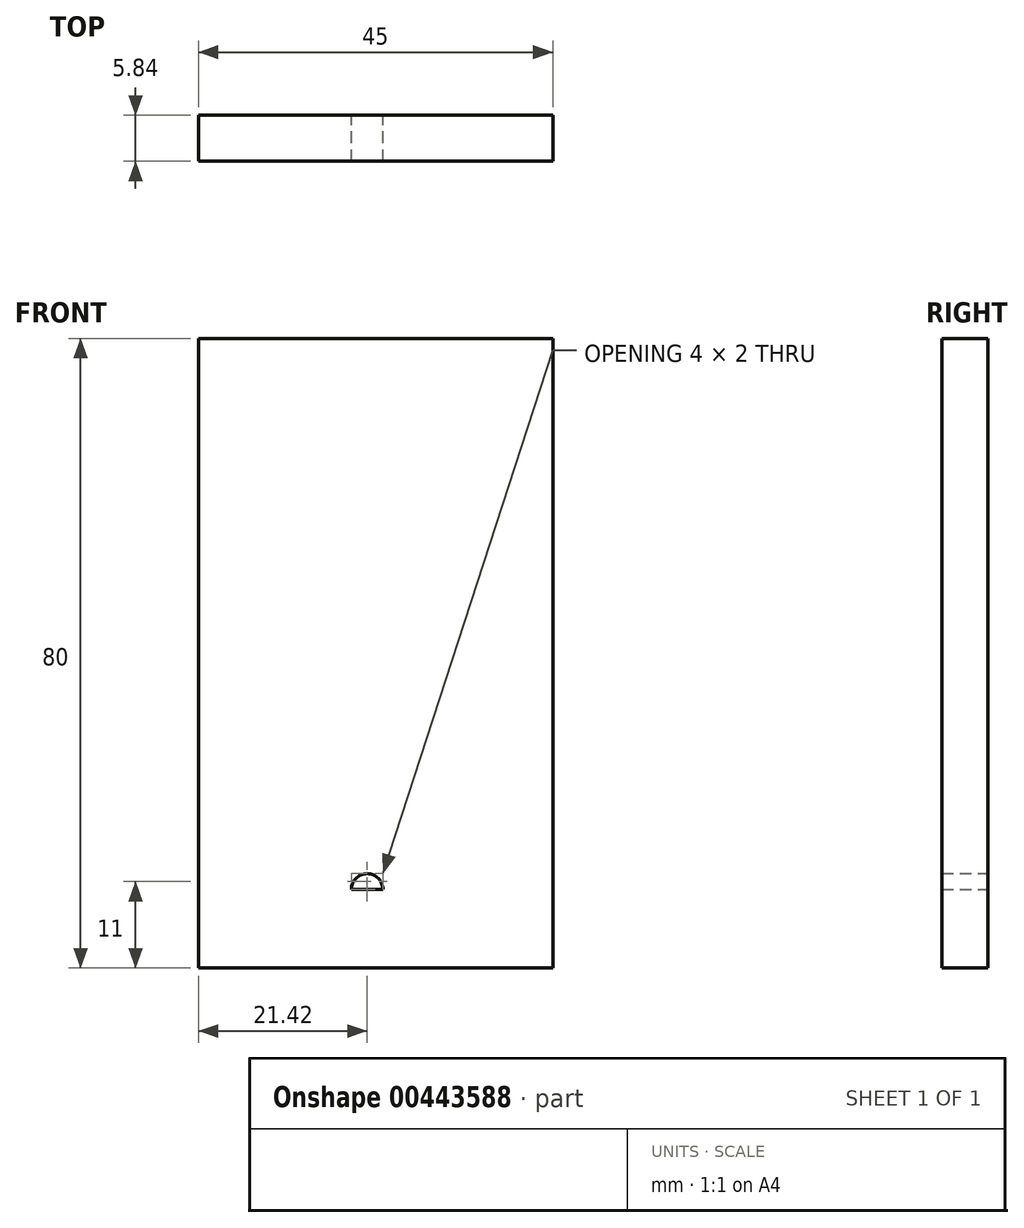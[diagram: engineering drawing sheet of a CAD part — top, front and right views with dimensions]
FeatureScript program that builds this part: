
annotation { "Feature Type Name" : "Feature", "Feature Type Description" : "" }
export const myFeature = defineFeature(function(context is Context, id is Id, definition is map)
    precondition{}
    {
        {
            var Q0;
            Q0=qCreatedBy(makeId("Front.planeOp"),FACE);
            var sketch = newSketch(context, id + "F0", { "sketchPlane" : qUnion([Q0])});
            skLineSegment(sketch, "E0.bottom", {"start": v(-21.42, 80) * mm, "end": v(23.58, 80) * mm});
            skLineSegment(sketch, "E0.top", {"start": v(-21.42, 0) * mm, "end": v(23.58, 0) * mm});
            skLineSegment(sketch, "E0.left", {"start": v(-21.42, 80) * mm, "end": v(-21.42, 0) * mm});
            skLineSegment(sketch, "E0.right", {"start": v(23.58, 80) * mm, "end": v(23.58, 0) * mm});
            skLineSegment(sketch, "E1", {"start": v(-132.92, 0) * mm, "end": v(0.73, 0) * mm});
            skArc(sketch, "E2", {"start": v(2, 10) * mm, "mid": v(0, 12) * mm, "end": v(-2, 10) * mm});
            skLineSegment(sketch, "E3", {"start": v(-2, 10) * mm, "end": v(2, 10) * mm});
            skSolve(sketch);
        }
        {
            var Q0;
            Q0=qSketchRegion(id+"F0",true);
            extrude(context, id + "F1", {"entities" : qUnion([Q0]), "depth" : 5.84 * mm});
        }
    });
